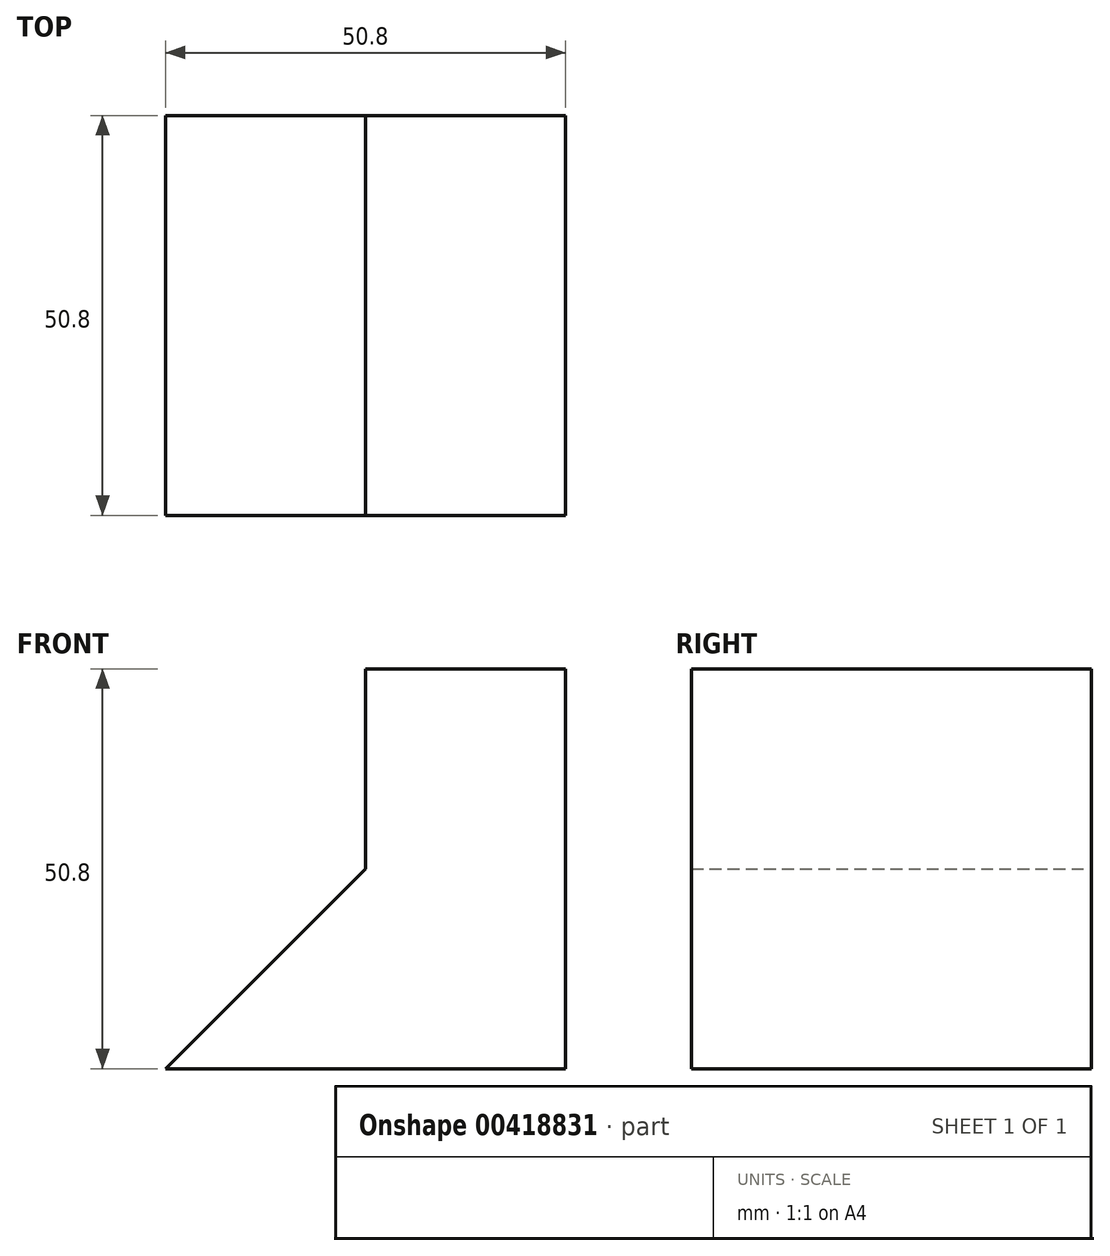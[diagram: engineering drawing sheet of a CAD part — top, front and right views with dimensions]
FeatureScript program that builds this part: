
annotation { "Feature Type Name" : "Feature", "Feature Type Description" : "" }
export const myFeature = defineFeature(function(context is Context, id is Id, definition is map)
    precondition{}
    {
        {
            var Q0;
            Q0=qCreatedBy(makeId("Front.planeOp"),FACE);
            var sketch = newSketch(context, id + "F0", { "sketchPlane" : qUnion([Q0])});
            skLineSegment(sketch, "E0", {"start": v(0, 0) * mm, "end": v(-50.8, 0) * mm});
            skLineSegment(sketch, "E1", {"start": v(0, 0) * mm, "end": v(0, 50.8) * mm});
            skLineSegment(sketch, "E2", {"start": v(0, 50.8) * mm, "end": v(-25.4, 50.8) * mm});
            skLineSegment(sketch, "E3", {"start": v(-25.4, 50.8) * mm, "end": v(-25.4, 25.4) * mm});
            skLineSegment(sketch, "E4", {"start": v(-25.4, 25.4) * mm, "end": v(-50.8, 0) * mm});
            skSolve(sketch);
        }
        {
            var Q0;
            Q0=makeQuery(id+"F0.imprint","IMPRINT",FACE,{"disambiguationData":[TD([[makeQuery(id+"F0.imprint","IMPRINT",EDGE,{"derivedFrom":sQuery(id+"F0.wireOp",EDGE,"E0")}),-1.0]])]});
            extrude(context, id + "F1", {"entities" : qUnion([Q0]), "depth" : 50.8 * mm});
        }
    });
